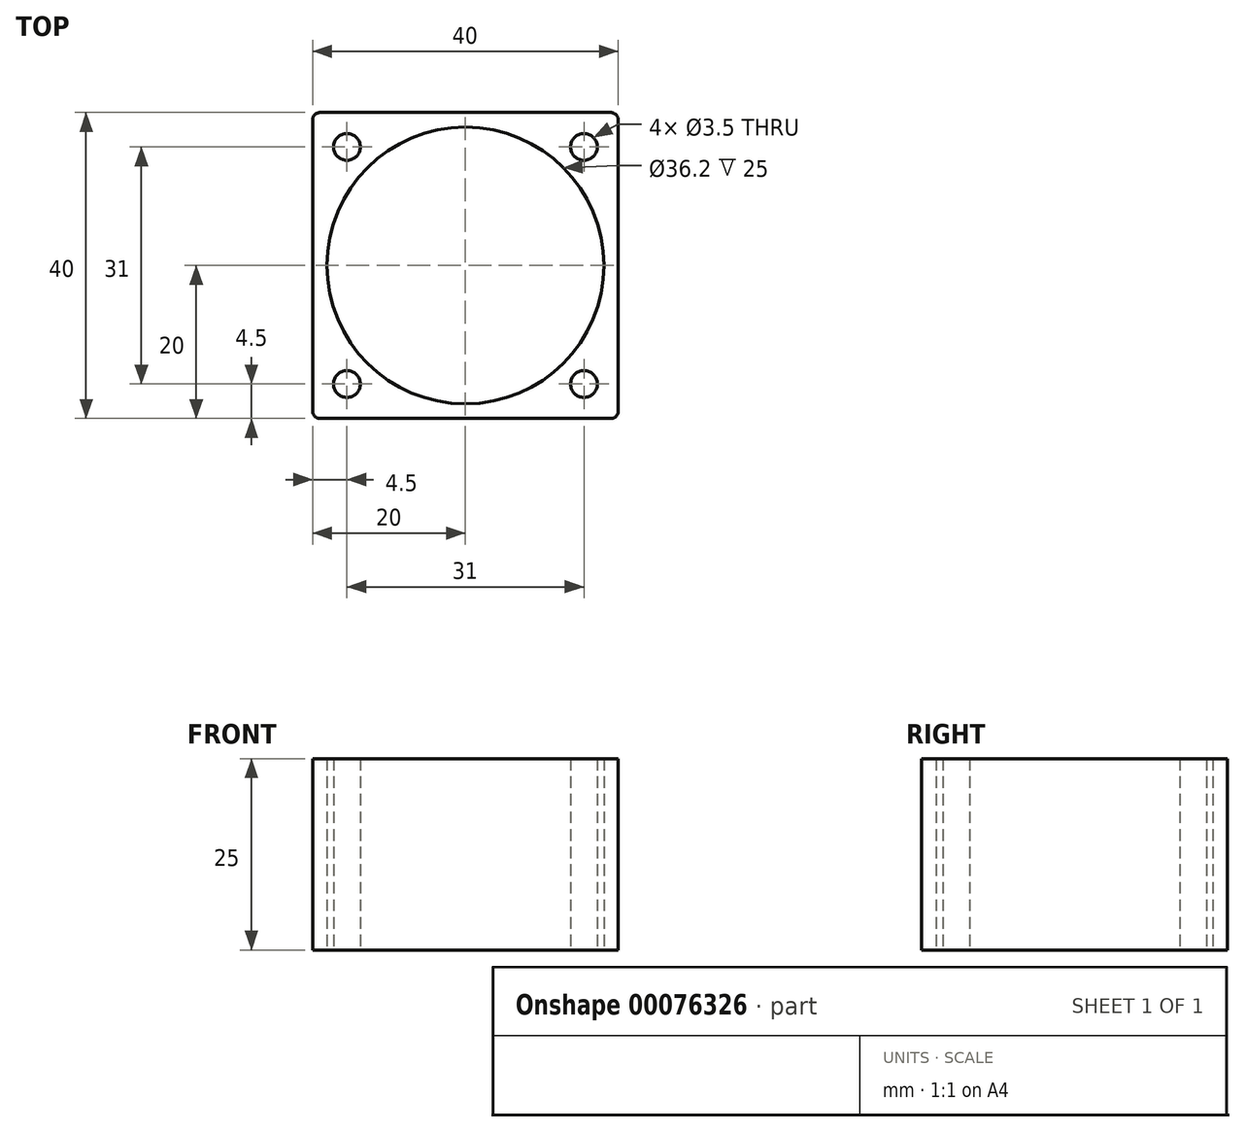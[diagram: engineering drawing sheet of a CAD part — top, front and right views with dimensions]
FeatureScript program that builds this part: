
annotation { "Feature Type Name" : "Feature", "Feature Type Description" : "" }
export const myFeature = defineFeature(function(context is Context, id is Id, definition is map)
    precondition{}
    {
        {
            var Q0;
            Q0=qCreatedBy(makeId("Top.planeOp"),FACE);
            var sketch = newSketch(context, id + "F0", { "sketchPlane" : qUnion([Q0])});
            skLineSegment(sketch, "E0.bottom", {"start": v(20, -20) * mm, "end": v(-20, -20) * mm});
            skLineSegment(sketch, "E0.top", {"start": v(20, 20) * mm, "end": v(-20, 20) * mm});
            skLineSegment(sketch, "E0.left", {"start": v(20, -20) * mm, "end": v(20, 20) * mm});
            skLineSegment(sketch, "E0.right", {"start": v(-20, -20) * mm, "end": v(-20, 20) * mm});
            skPoint(sketch, "E0.middle", {"position": v(0, 0) * mm});
            skCircle(sketch, "E1", {"center": v(-15.5, 15.5) * mm, "radius": 1.75 * mm});
            skCircle(sketch, "E2", {"center": v(15.5, 15.5) * mm, "radius": 1.75 * mm});
            skCircle(sketch, "E3", {"center": v(15.5, -15.5) * mm, "radius": 1.75 * mm});
            skCircle(sketch, "E4", {"center": v(-15.5, -15.5) * mm, "radius": 1.75 * mm});
            skCircle(sketch, "E5", {"center": v(0, 0) * mm, "radius": 18.1 * mm});
            skSolve(sketch);
        }
        {
            var Q0;
            Q0=makeQuery(id+"F0.imprint","IMPRINT",FACE,{"disambiguationData":[TD([[makeQuery(id+"F0.imprint","IMPRINT",EDGE,{"derivedFrom":sQuery(id+"F0.wireOp",EDGE,"E0.bottom")}),-1.0]])]});
            extrude(context, id + "F1", {"entities" : qUnion([Q0]), "depth" : 25 * mm});
        }
        {
            var Q0;
            Q0=makeQuery(id+"F1.opExtrude","SWEPT_EDGE",EDGE,{"disambiguationData":[OSD([sQuery(id+"F0.wireOp",EDGE,"E0.bottom"),sQuery(id+"F0.wireOp",EDGE,"E0.right")])]});
            var Q1;
            Q1=makeQuery(id+"F1.opExtrude","SWEPT_EDGE",EDGE,{"disambiguationData":[OSD([sQuery(id+"F0.wireOp",EDGE,"E0.bottom"),sQuery(id+"F0.wireOp",EDGE,"E0.left")])]});
            var Q2;
            Q2=makeQuery(id+"F1.opExtrude","SWEPT_EDGE",EDGE,{"disambiguationData":[OSD([sQuery(id+"F0.wireOp",EDGE,"E0.top"),sQuery(id+"F0.wireOp",EDGE,"E0.left")])]});
            var Q3;
            Q3=makeQuery(id+"F1.opExtrude","SWEPT_EDGE",EDGE,{"disambiguationData":[OSD([sQuery(id+"F0.wireOp",EDGE,"E0.top"),sQuery(id+"F0.wireOp",EDGE,"E0.right")])]});
            fillet(context, id + "F2", {"entities" : qUnion([Q0, Q1, Q2, Q3]), "radius" : 1 * mm, "tangentPropagation" : true, "allowEdgeOverflow" : false});
        }
    });
